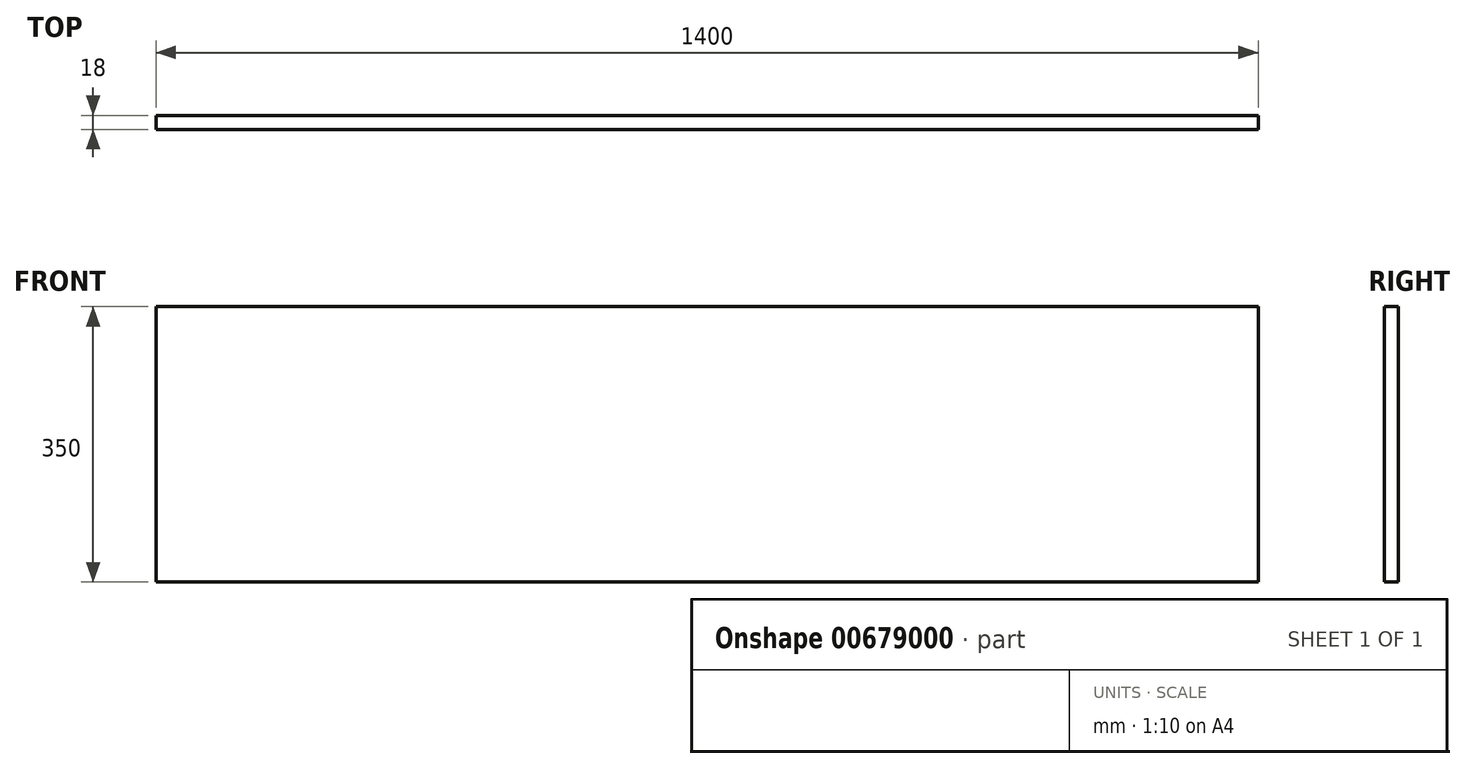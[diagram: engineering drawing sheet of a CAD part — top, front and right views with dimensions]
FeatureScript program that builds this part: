
annotation { "Feature Type Name" : "Feature", "Feature Type Description" : "" }
export const myFeature = defineFeature(function(context is Context, id is Id, definition is map)
    precondition{}
    {
        {
            var Q0;
            Q0=qCreatedBy(makeId("Front.planeOp"),FACE);
            var sketch = newSketch(context, id + "F0", { "sketchPlane" : qUnion([Q0])});
            skLineSegment(sketch, "E0.bottom", {"start": v(-700, -175) * mm, "end": v(700, -175) * mm});
            skLineSegment(sketch, "E0.top", {"start": v(-700, 175) * mm, "end": v(700, 175) * mm});
            skLineSegment(sketch, "E0.left", {"start": v(-700, -175) * mm, "end": v(-700, 175) * mm});
            skLineSegment(sketch, "E0.right", {"start": v(700, -175) * mm, "end": v(700, 175) * mm});
            skPoint(sketch, "E0.middle", {"position": v(0, 0) * mm});
            skSolve(sketch);
        }
        {
            var Q0;
            Q0=makeQuery(id+"F0.imprint","IMPRINT",FACE,{"disambiguationData":[TD([[makeQuery(id+"F0.imprint","IMPRINT",EDGE,{"derivedFrom":sQuery(id+"F0.wireOp",EDGE,"E0.bottom")}),1.0]])]});
            extrude(context, id + "F1", {"entities" : qUnion([Q0]), "oppositeDirection" : true, "depth" : 18 * mm, "offsetDistance" : 25 * mm});
        }
    });
